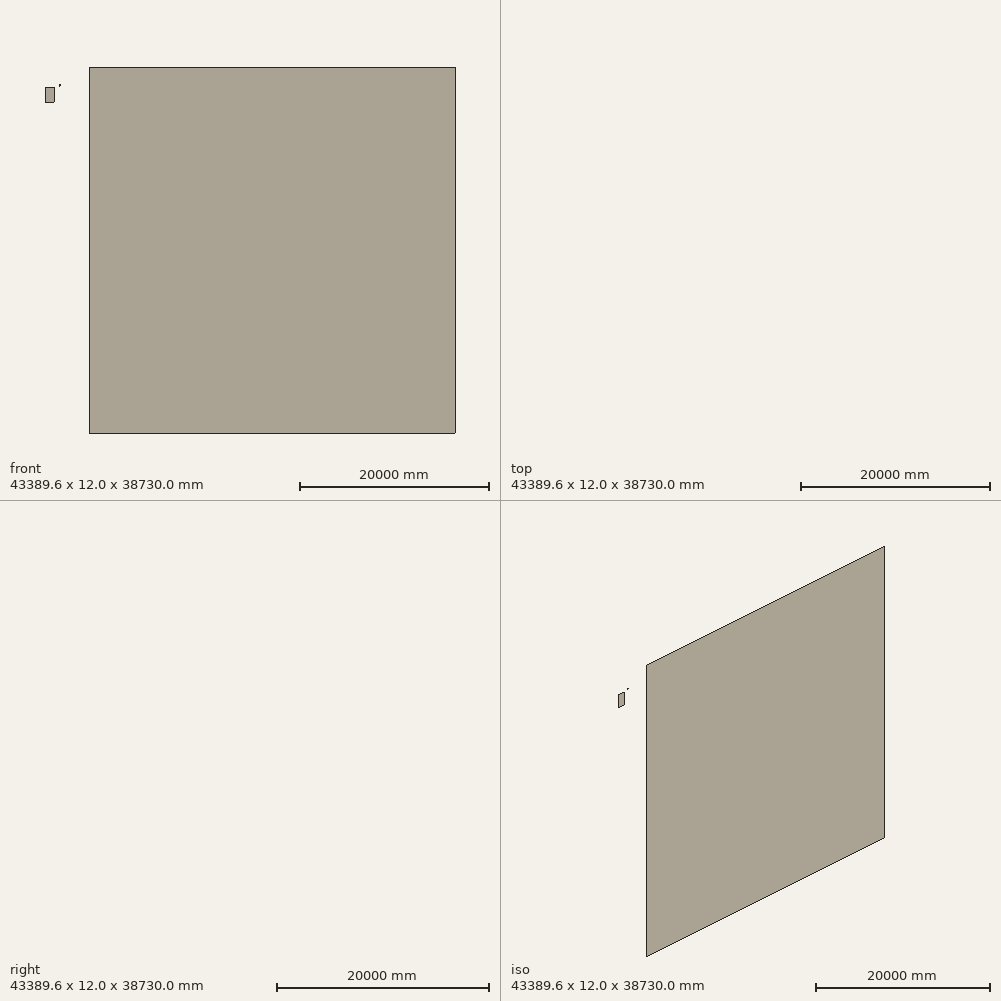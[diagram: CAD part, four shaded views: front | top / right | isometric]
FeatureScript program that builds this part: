
annotation { "Feature Type Name" : "Feature", "Feature Type Description" : "" }
export const myFeature = defineFeature(function(context is Context, id is Id, definition is map)
    precondition{}
    {
        {
            var Q0;
            Q0=qCreatedBy(makeId("Front.planeOp"),FACE);
            var sketch = newSketch(context, id + "F0", { "sketchPlane" : qUnion([Q0])});
            skLineSegment(sketch, "E0", {"start": v(1286.74, 1046.2) * mm, "end": v(2276.74, 1046.2) * mm});
            skLineSegment(sketch, "E1", {"start": v(2276.74, -476.4) * mm, "end": v(1286.74, -476.4) * mm});
            skLineSegment(sketch, "E2", {"start": v(1286.74, 1046.2) * mm, "end": v(1286.74, -476.4) * mm});
            skLineSegment(sketch, "E3", {"start": v(2276.74, 1046.2) * mm, "end": v(2276.74, -476.4) * mm});
            skSolve(sketch);
        }
        {
            var Q0;
            Q0=makeQuery(id+"F0.imprint","IMPRINT",FACE,{"disambiguationData":[TD([[makeQuery(id+"F0.imprint","IMPRINT",EDGE,{"derivedFrom":sQuery(id+"F0.wireOp",EDGE,"E0")}),-1.0]])]});
            var sketch = newSketch(context, id + "F1", { "sketchPlane" : qUnion([Q0])});
            skLineSegment(sketch, "E4.bottom", {"start": v(766.3, 681.77) * mm, "end": v(892.3, 681.77) * mm});
            skLineSegment(sketch, "E4.top", {"start": v(766.3, 525.77) * mm, "end": v(892.3, 525.77) * mm});
            skLineSegment(sketch, "E4.left", {"start": v(751.3, 666.77) * mm, "end": v(751.3, 540.77) * mm});
            skLineSegment(sketch, "E4.right", {"start": v(907.3, 666.77) * mm, "end": v(907.3, 540.77) * mm});
            skPoint(sketch, "E5.visualSharp", {"position": v(751.3, 681.77) * mm});
            skArc(sketch, "E5.filletArc", {"start": v(766.3, 681.77) * mm, "mid": v(755.7, 677.38) * mm, "end": v(751.3, 666.77) * mm});
            skPoint(sketch, "E6.visualSharp", {"position": v(907.3, 681.77) * mm});
            skArc(sketch, "E6.filletArc", {"start": v(907.3, 666.77) * mm, "mid": v(902.9, 677.38) * mm, "end": v(892.3, 681.77) * mm});
            skPoint(sketch, "E7.visualSharp", {"position": v(907.3, 525.77) * mm});
            skArc(sketch, "E7.filletArc", {"start": v(892.3, 525.77) * mm, "mid": v(902.9, 530.16) * mm, "end": v(907.3, 540.77) * mm});
            skPoint(sketch, "E8.visualSharp", {"position": v(751.3, 525.77) * mm});
            skArc(sketch, "E8.filletArc", {"start": v(751.3, 540.77) * mm, "mid": v(755.7, 530.16) * mm, "end": v(766.3, 525.77) * mm});
            skLineSegment(sketch, "E9.bottom", {"start": v(3038.85, 81858.35) * mm, "end": v(2869.38, 81858.35) * mm});
            skLineSegment(sketch, "E9.top", {"start": v(3038.85, 72650.5) * mm, "end": v(2869.38, 72650.5) * mm});
            skLineSegment(sketch, "E9.left", {"start": v(3038.85, 81858.35) * mm, "end": v(3038.85, 72650.5) * mm});
            skLineSegment(sketch, "E9.right", {"start": v(2869.38, 81858.35) * mm, "end": v(2869.38, 72650.5) * mm});
            skSolve(sketch);
        }
        {
            var Q0;
            Q0=makeQuery(id+"F1.imprint","IMPRINT",FACE,{"disambiguationData":[TD([[makeQuery(id+"F1.imprint","IMPRINT",EDGE,{"derivedFrom":sQuery(id+"F1.wireOp",EDGE,"E4.bottom")}),-1.0]])]});
            extrude(context, id + "F2", {"entities" : qUnion([Q0]), "depth" : 1 * mm, "offsetDistance" : 25 * mm});
        }
        {
            var Q0;
            Q0=makeQuery(id+"F2.opExtrude","CAP_FACE",FACE,{"disambiguationData":[OSD([sQuery(id+"F1.wireOp",EDGE,"E4.bottom"),sQuery(id+"F1.wireOp",EDGE,"E4.top"),sQuery(id+"F1.wireOp",EDGE,"E4.left"),sQuery(id+"F1.wireOp",EDGE,"E4.right"),sQuery(id+"F1.wireOp",EDGE,"E5.filletArc"),sQuery(id+"F1.wireOp",EDGE,"E6.filletArc"),sQuery(id+"F1.wireOp",EDGE,"E7.filletArc"),sQuery(id+"F1.wireOp",EDGE,"E8.filletArc")])],"isStart":false});
            var sketch = newSketch(context, id + "F3", { "sketchPlane" : qUnion([Q0])});
            skLineSegment(sketch, "E10.bottom", {"start": v(1068.35, 691.33) * mm, "end": v(1072.64, 691.33) * mm});
            skLineSegment(sketch, "E10.top", {"start": v(1068.35, 535.33) * mm, "end": v(1072.64, 535.33) * mm});
            skLineSegment(sketch, "E10.left", {"start": v(1068.35, 691.33) * mm, "end": v(1068.35, 535.33) * mm});
            skLineSegment(sketch, "E10.right", {"start": v(1072.64, 691.33) * mm, "end": v(1072.64, 535.33) * mm});
            skLineSegment(sketch, "E11.bottom", {"start": v(1040.3, 699.13) * mm, "end": v(1044.6, 699.13) * mm});
            skLineSegment(sketch, "E11.top", {"start": v(1040.3, 543.13) * mm, "end": v(1044.6, 543.13) * mm});
            skLineSegment(sketch, "E11.left", {"start": v(1040.3, 699.13) * mm, "end": v(1040.3, 543.13) * mm});
            skLineSegment(sketch, "E11.right", {"start": v(1044.6, 699.13) * mm, "end": v(1044.6, 543.13) * mm});
            skLineSegment(sketch, "E12.bottom", {"start": v(997.94, 678.37) * mm, "end": v(1002.23, 678.37) * mm});
            skLineSegment(sketch, "E12.top", {"start": v(997.94, 522.37) * mm, "end": v(1002.23, 522.37) * mm});
            skLineSegment(sketch, "E12.left", {"start": v(997.94, 678.37) * mm, "end": v(997.94, 522.37) * mm});
            skLineSegment(sketch, "E12.right", {"start": v(1002.23, 678.37) * mm, "end": v(1002.23, 522.37) * mm});
            skSolve(sketch);
        }
        {
            var Q0;
            Q0=makeQuery(id+"F3.imprint","IMPRINT",FACE,{"disambiguationData":[TD([[makeQuery(id+"F3.imprint","IMPRINT",EDGE,{"derivedFrom":sQuery(id+"F3.wireOp",EDGE,"E10.bottom")}),-1.0]])]});
            var Q1;
            Q1=makeQuery(id+"F3.imprint","IMPRINT",FACE,{"disambiguationData":[TD([[makeQuery(id+"F3.imprint","IMPRINT",EDGE,{"derivedFrom":sQuery(id+"F3.wireOp",EDGE,"E11.bottom")}),-1.0]])]});
            var Q2;
            Q2=makeQuery(id+"F3.imprint","IMPRINT",FACE,{"disambiguationData":[TD([[makeQuery(id+"F3.imprint","IMPRINT",EDGE,{"derivedFrom":sQuery(id+"F3.wireOp",EDGE,"E12.bottom")}),-1.0]])]});
            extrude(context, id + "F4", {"entities" : qUnion([Q0, Q1, Q2]), "depth" : 0.5 * mm, "offsetDistance" : 25 * mm});
        }
        {
            var Q0;
            Q0=makeQuery(id+"F4.opExtrude","SWEPT_BODY",BODY,{"disambiguationData":[OSD([sQuery(id+"F3.wireOp",EDGE,"E12.bottom"),sQuery(id+"F3.wireOp",EDGE,"E12.top"),sQuery(id+"F3.wireOp",EDGE,"E12.left"),sQuery(id+"F3.wireOp",EDGE,"E12.right")])]});
            transform(context, id + "F5", {"entities" : qUnion([Q0]), "transformType" : TransformType.TRANSLATION_3D, "dx" : -232.8 * mm, "dy" : 0 * mm, "dz" : 3.3 * mm, "makeCopy" : false});
        }
        {
            var Q0;
            Q0=makeQuery(id+"F4.opExtrude","SWEPT_BODY",BODY,{"disambiguationData":[OSD([sQuery(id+"F3.wireOp",EDGE,"E12.bottom"),sQuery(id+"F3.wireOp",EDGE,"E12.top"),sQuery(id+"F3.wireOp",EDGE,"E12.left"),sQuery(id+"F3.wireOp",EDGE,"E12.right")])]});
            transform(context, id + "F6", {"entities" : qUnion([Q0]), "transformType" : TransformType.TRANSLATION_3D, "dx" : 6E-4000 * mm, "dy" : 0 * mm, "dz" : 0 * mm, "makeCopy" : false});
        }
        {
            var Q0;
            Q0=makeQuery(id+"F4.opExtrude","SWEPT_BODY",BODY,{"disambiguationData":[OSD([sQuery(id+"F3.wireOp",EDGE,"E12.bottom"),sQuery(id+"F3.wireOp",EDGE,"E12.top"),sQuery(id+"F3.wireOp",EDGE,"E12.left"),sQuery(id+"F3.wireOp",EDGE,"E12.right")])]});
            var Q1;
            Q1=makeQuery(id+"F4.opExtrude","CAP_VERTEX",VERTEX,{"disambiguationData":[OSD([sQuery(id+"F3.wireOp",EDGE,"E12.top"),sQuery(id+"F3.wireOp",EDGE,"E12.left")])],"isStart":false});
            var Q2;
            Q2=makeQuery(id+"F2.opExtrude","CAP_EDGE",EDGE,{"disambiguationData":[OSD([sQuery(id+"F1.wireOp",EDGE,"E4.top")])],"isStart":false});
            transform(context, id + "F7", {"entities" : qUnion([Q0]), "transformType" : TransformType.TRANSLATION_ENTITY, "oppositeDirectionEntity" : false, "transformLine" : qUnion([Q1, Q2]), "makeCopy" : false});
        }
        {
            var Q0;
            Q0=makeQuery(id+"F4.opExtrude","SWEPT_BODY",BODY,{"disambiguationData":[OSD([sQuery(id+"F3.wireOp",EDGE,"E12.bottom"),sQuery(id+"F3.wireOp",EDGE,"E12.top"),sQuery(id+"F3.wireOp",EDGE,"E12.left"),sQuery(id+"F3.wireOp",EDGE,"E12.right")])]});
            var Q1;
            Q1=makeQuery(id+"F4.opExtrude","CAP_VERTEX",VERTEX,{"disambiguationData":[OSD([sQuery(id+"F3.wireOp",EDGE,"E12.bottom"),sQuery(id+"F3.wireOp",EDGE,"E12.right")])],"isStart":true});
            var Q2;
            Q2=makeQuery(id+"F2.opExtrude","CAP_VERTEX",VERTEX,{"disambiguationData":[OSD([sQuery(id+"F1.wireOp",EDGE,"E4.bottom"),sQuery(id+"F1.wireOp",EDGE,"E6.filletArc")])],"isStart":false});
            transform(context, id + "F8", {"entities" : qUnion([Q0]), "transformType" : TransformType.TRANSLATION_ENTITY, "oppositeDirectionEntity" : false, "transformLine" : qUnion([Q1, Q2]), "makeCopy" : false});
        }
        {
            var Q0;
            Q0=makeQuery(id+"F4.opExtrude","SWEPT_BODY",BODY,{"disambiguationData":[OSD([sQuery(id+"F3.wireOp",EDGE,"E11.bottom"),sQuery(id+"F3.wireOp",EDGE,"E11.top"),sQuery(id+"F3.wireOp",EDGE,"E11.left"),sQuery(id+"F3.wireOp",EDGE,"E11.right")])]});
            var Q1;
            Q1=sQuery(id+"F3.wireOp",VERTEX,"E11.bottom.start");
            var Q2;
            Q2=makeQuery(id+"F2.opExtrude","CAP_VERTEX",VERTEX,{"disambiguationData":[OSD([sQuery(id+"F1.wireOp",EDGE,"E4.bottom"),sQuery(id+"F1.wireOp",EDGE,"E5.filletArc")])],"isStart":false});
            transform(context, id + "F9", {"entities" : qUnion([Q0]), "transformType" : TransformType.TRANSLATION_ENTITY, "oppositeDirectionEntity" : false, "transformLine" : qUnion([Q1, Q2]), "makeCopy" : false});
        }
        {
            var Q0;
            Q0=sQuery(id+"F3.wireOp",EDGE,"E10.bottom");
            cPoint(context, id + "F10", {"entities" : qUnion([Q0]), "parameter" : 0.5});
        }
        {
            var Q0;
            Q0=makeQuery(id+"F2.opExtrude","CAP_EDGE",EDGE,{"disambiguationData":[OSD([sQuery(id+"F1.wireOp",EDGE,"E4.bottom")])],"isStart":false});
            cPoint(context, id + "F11", {"entities" : qUnion([Q0]), "parameter" : 0.5});
        }
        {
            var Q0;
            Q0=makeQuery(id+"F4.opExtrude","SWEPT_BODY",BODY,{"disambiguationData":[OSD([sQuery(id+"F3.wireOp",EDGE,"E10.bottom"),sQuery(id+"F3.wireOp",EDGE,"E10.top"),sQuery(id+"F3.wireOp",EDGE,"E10.left"),sQuery(id+"F3.wireOp",EDGE,"E10.right")])]});
            var Q1;
            Q1=qCreatedBy(id+"F10",VERTEX);
            var Q2;
            Q2=qCreatedBy(id+"F11",VERTEX);
            transform(context, id + "F12", {"entities" : qUnion([Q0]), "transformType" : TransformType.TRANSLATION_ENTITY, "oppositeDirectionEntity" : false, "transformLine" : qUnion([Q1, Q2]), "makeCopy" : false});
        }
        {
            var Q0;
            Q0=qCreatedBy(makeId("Front.planeOp"),FACE);
            var sketch = newSketch(context, id + "F13", { "sketchPlane" : qUnion([Q0])});
            skLineSegment(sketch, "E13.bottom", {"start": v(-721, 443.66) * mm, "end": v(269, 443.66) * mm});
            skLineSegment(sketch, "E13.top", {"start": v(-721, -1231.34) * mm, "end": v(269, -1231.34) * mm});
            skLineSegment(sketch, "E13.left", {"start": v(-721, 443.66) * mm, "end": v(-721, -1231.34) * mm});
            skLineSegment(sketch, "E13.right", {"start": v(269, 443.66) * mm, "end": v(269, -1231.34) * mm});
            skSolve(sketch);
        }
        {
            var Q0;
            Q0=makeQuery(id+"F13.imprint","IMPRINT",FACE,{"disambiguationData":[TD([[makeQuery(id+"F13.imprint","IMPRINT",EDGE,{"derivedFrom":sQuery(id+"F13.wireOp",EDGE,"E13.bottom")}),-1.0]])]});
            extrude(context, id + "F14", {"entities" : qUnion([Q0]), "depth" : 2 * mm, "offsetDistance" : 25 * mm});
        }
        {
            var Q0;
            Q0=makeQuery(id+"F14.opExtrude","CAP_FACE",FACE,{"disambiguationData":[OSD([sQuery(id+"F13.wireOp",EDGE,"E13.bottom"),sQuery(id+"F13.wireOp",EDGE,"E13.top"),sQuery(id+"F13.wireOp",EDGE,"E13.left"),sQuery(id+"F13.wireOp",EDGE,"E13.right")])],"isStart":false});
            var sketch = newSketch(context, id + "F15", { "sketchPlane" : qUnion([Q0])});
            skLineSegment(sketch, "E14.bottom", {"start": v(3938.56, 2523.51) * mm, "end": v(42668.56, 2523.51) * mm});
            skLineSegment(sketch, "E14.top", {"start": v(3938.56, -36206.49) * mm, "end": v(42668.56, -36206.49) * mm});
            skLineSegment(sketch, "E14.left", {"start": v(3938.56, 2523.51) * mm, "end": v(3938.56, -36206.49) * mm});
            skLineSegment(sketch, "E14.right", {"start": v(42668.56, 2523.51) * mm, "end": v(42668.56, -36206.49) * mm});
            skSolve(sketch);
        }
        {
            var Q0;
            Q0=makeQuery(id+"F15.imprint","IMPRINT",FACE,{"disambiguationData":[TD([[makeQuery(id+"F15.imprint","IMPRINT",EDGE,{"derivedFrom":sQuery(id+"F15.wireOp",EDGE,"E14.bottom")}),-1.0]])]});
            extrude(context, id + "F16", {"entities" : qUnion([Q0]), "depth" : 10 * mm, "offsetDistance" : 25 * mm});
        }
    });
